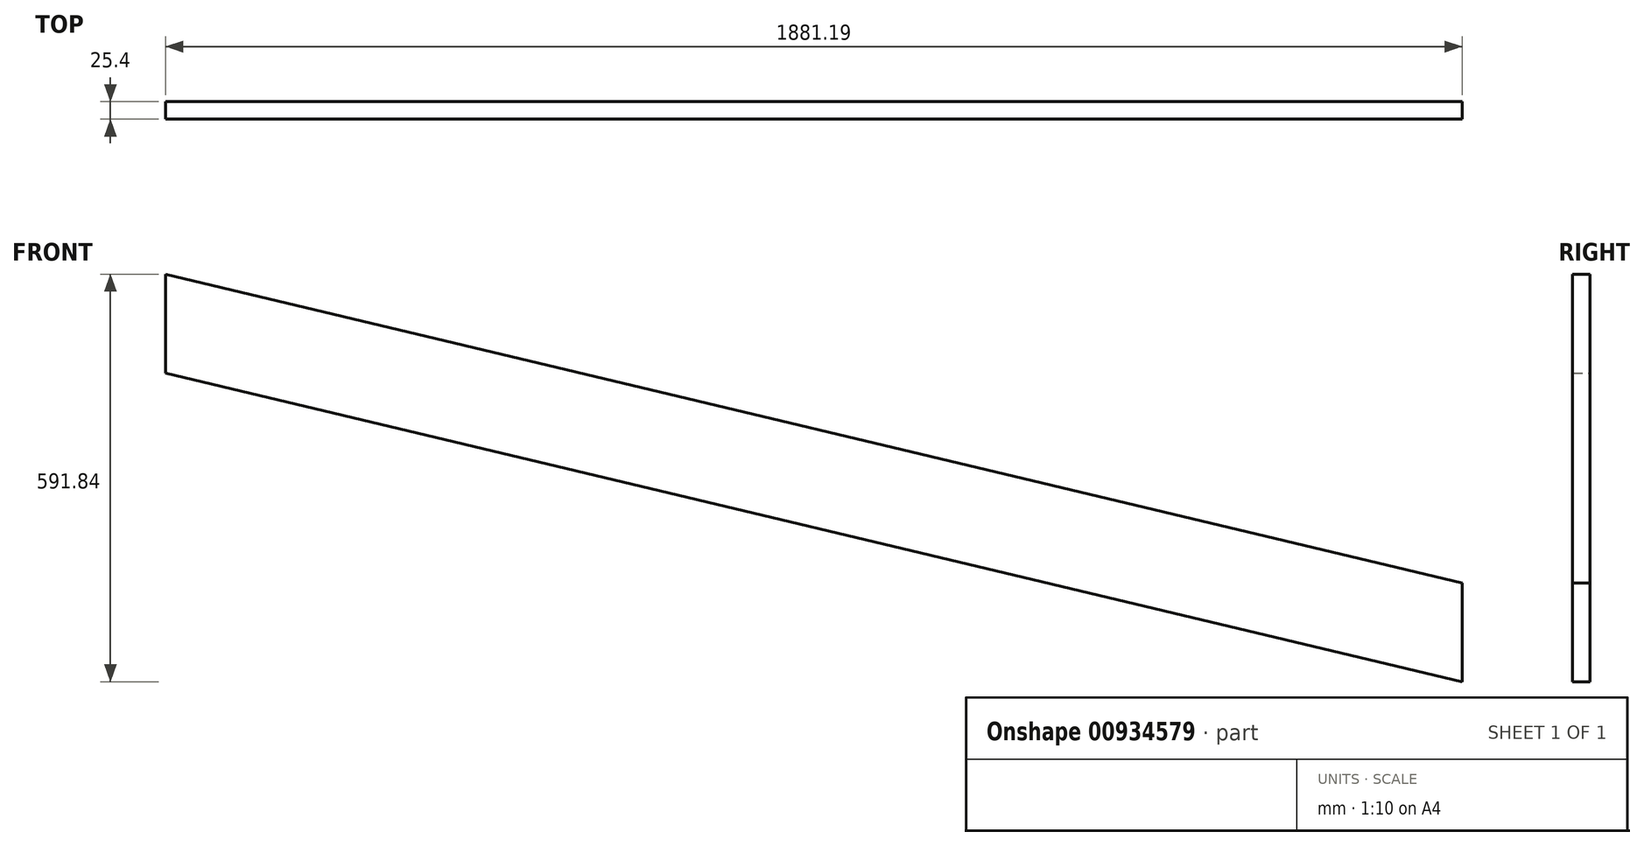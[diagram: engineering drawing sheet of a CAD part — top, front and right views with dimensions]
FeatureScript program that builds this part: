
annotation { "Feature Type Name" : "Feature", "Feature Type Description" : "" }
export const myFeature = defineFeature(function(context is Context, id is Id, definition is map)
    precondition{}
    {
        {
            var Q0;
            Q0=qCreatedBy(makeId("Front.planeOp"),FACE);
            var sketch = newSketch(context, id + "F0", { "sketchPlane" : qUnion([Q0])});
            skLineSegment(sketch, "E0", {"start": v(4838.76, -591.84) * mm, "end": v(2957.57, -143.61) * mm});
            skLineSegment(sketch, "E1.0", {"start": v(4838.76, -448.23) * mm, "end": v(2957.57, 0) * mm});
            skLineSegment(sketch, "E2", {"start": v(4838.76, -591.84) * mm, "end": v(4838.76, -448.23) * mm});
            skLineSegment(sketch, "E3", {"start": v(2957.57, 0) * mm, "end": v(2957.57, -143.61) * mm});
            skSolve(sketch);
        }
        {
            var Q0;
            Q0=makeQuery(id+"F0.imprint","IMPRINT",FACE,{"disambiguationData":[TD([[makeQuery(id+"F0.imprint","IMPRINT",EDGE,{"derivedFrom":sQuery(id+"F0.wireOp",EDGE,"E0")}),-1.0]])]});
            extrude(context, id + "F1", {"entities" : qUnion([Q0]), "depth" : 25.4 * mm, "offsetDistance" : 25.4 * mm});
        }
    });
